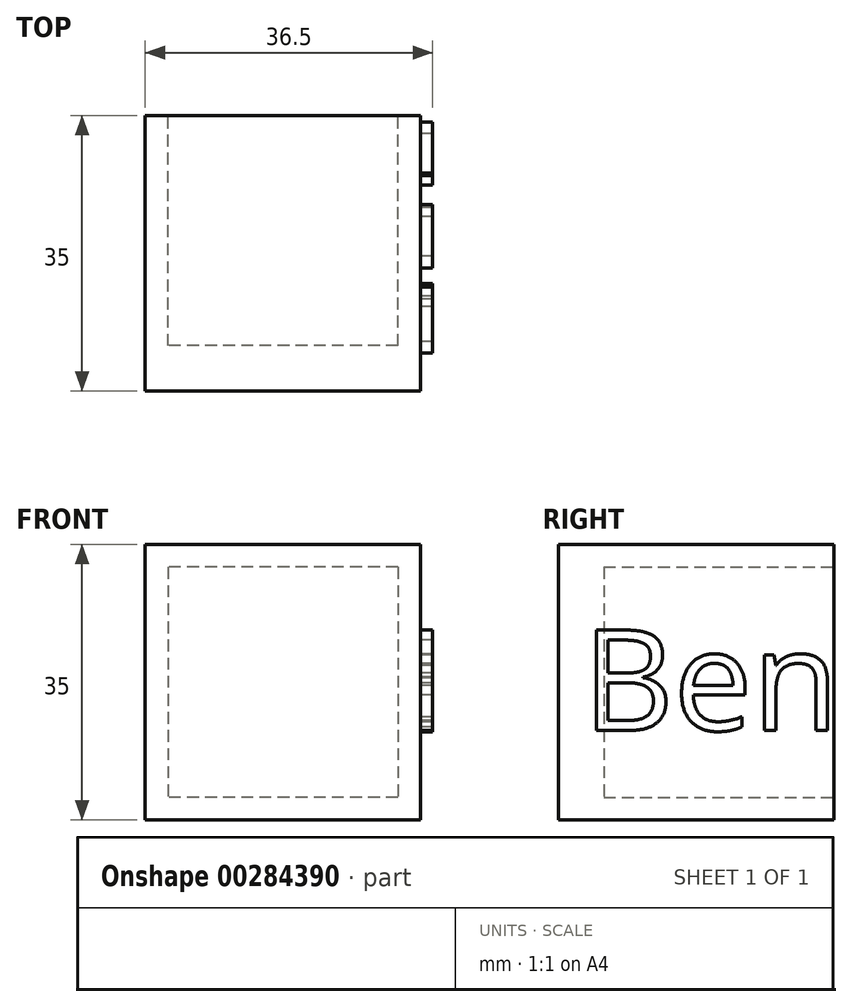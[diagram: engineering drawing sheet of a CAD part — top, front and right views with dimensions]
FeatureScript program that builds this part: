
annotation { "Feature Type Name" : "Feature", "Feature Type Description" : "" }
export const myFeature = defineFeature(function(context is Context, id is Id, definition is map)
    precondition{}
    {
        {
            var Q0;
            Q0=qCreatedBy(makeId("Front.planeOp"),FACE);
            var sketch = newSketch(context, id + "F0", { "sketchPlane" : qUnion([Q0])});
            skLineSegment(sketch, "E0.bottom", {"start": v(17.5, 17.5) * mm, "end": v(-17.5, 17.5) * mm});
            skLineSegment(sketch, "E0.top", {"start": v(17.5, -17.5) * mm, "end": v(-17.5, -17.5) * mm});
            skLineSegment(sketch, "E0.left", {"start": v(17.5, 17.5) * mm, "end": v(17.5, -17.5) * mm});
            skLineSegment(sketch, "E0.right", {"start": v(-17.5, 17.5) * mm, "end": v(-17.5, -17.5) * mm});
            skPoint(sketch, "E0.middle", {"position": v(0, 0) * mm});
            skSolve(sketch);
        }
        {
            var Q0;
            Q0=makeQuery(id+"F0.imprint","IMPRINT",FACE,{"disambiguationData":[TD([[makeQuery(id+"F0.imprint","IMPRINT",EDGE,{"derivedFrom":sQuery(id+"F0.wireOp",EDGE,"E0.bottom")}),1.0]])]});
            extrude(context, id + "F1", {"entities" : qUnion([Q0]), "depth" : 35 * mm});
        }
        {
            var Q0;
            Q0=qCreatedBy(makeId("Front.planeOp"),FACE);
            var sketch = newSketch(context, id + "F2", { "sketchPlane" : qUnion([Q0])});
            skLineSegment(sketch, "E1.bottom", {"start": v(14.62, 14.62) * mm, "end": v(-14.62, 14.62) * mm});
            skLineSegment(sketch, "E1.top", {"start": v(14.62, -14.62) * mm, "end": v(-14.62, -14.62) * mm});
            skLineSegment(sketch, "E1.left", {"start": v(14.62, 14.62) * mm, "end": v(14.62, -14.62) * mm});
            skLineSegment(sketch, "E1.right", {"start": v(-14.62, 14.62) * mm, "end": v(-14.62, -14.62) * mm});
            skPoint(sketch, "E1.middle", {"position": v(0, 0) * mm});
            skSolve(sketch);
        }
        {
            var Q0;
            Q0 = qSketchRegion(id + "F2", true);
            extrude(context, id + "F3", {"entities" : qUnion([Q0]), "operationType" : NewBodyOperationType.REMOVE, "depth" : 29.24 * mm});
        }
        {
            var Q0;
            Q0=makeQuery(id+"F1.opExtrude","SWEPT_FACE",FACE,{"disambiguationData":[OSD([sQuery(id+"F0.wireOp",EDGE,"E0.left")])]});
            var sketch = newSketch(context, id + "F4", { "sketchPlane" : qUnion([Q0])});
            skText(sketch, "E2", { "text": "Ben", "fontName": "OpenSans-Regular.ttf"});
            const initialGuessF4  = {"E2": [-0.03193, -0.00611, 1, 0, 0.01285]};
            skSetInitialGuess(sketch, initialGuessF4);
            skSolve(sketch);
        }
        {
            var Q0;
            Q0=makeQuery(id+"F4.imprint","IMPRINT",FACE,{"disambiguationData":[TD([[makeQuery(id+"F4.imprint","IMPRINT",EDGE,{"derivedFrom":sQuery(id+"F4.wireOp",EDGE,"E2.sketch_text.stroke-44")}),-1.0]])]});
            var Q1;
            Q1=makeQuery(id+"F4.imprint","IMPRINT",FACE,{"disambiguationData":[TD([[makeQuery(id+"F4.imprint","IMPRINT",EDGE,{"derivedFrom":sQuery(id+"F4.wireOp",EDGE,"E2.sketch_text.stroke-25")}),-1.0]])]});
            var Q2;
            Q2=makeQuery(id+"F4.imprint","IMPRINT",FACE,{"disambiguationData":[TD([[makeQuery(id+"F4.imprint","IMPRINT",EDGE,{"derivedFrom":sQuery(id+"F4.wireOp",EDGE,"E2.sketch_text.stroke-0")}),-1.0]])]});
            extrude(context, id + "F5", {"entities" : qUnion([Q0, Q1, Q2]), "operationType" : NewBodyOperationType.ADD, "depth" : 1.5 * mm});
        }
    });
